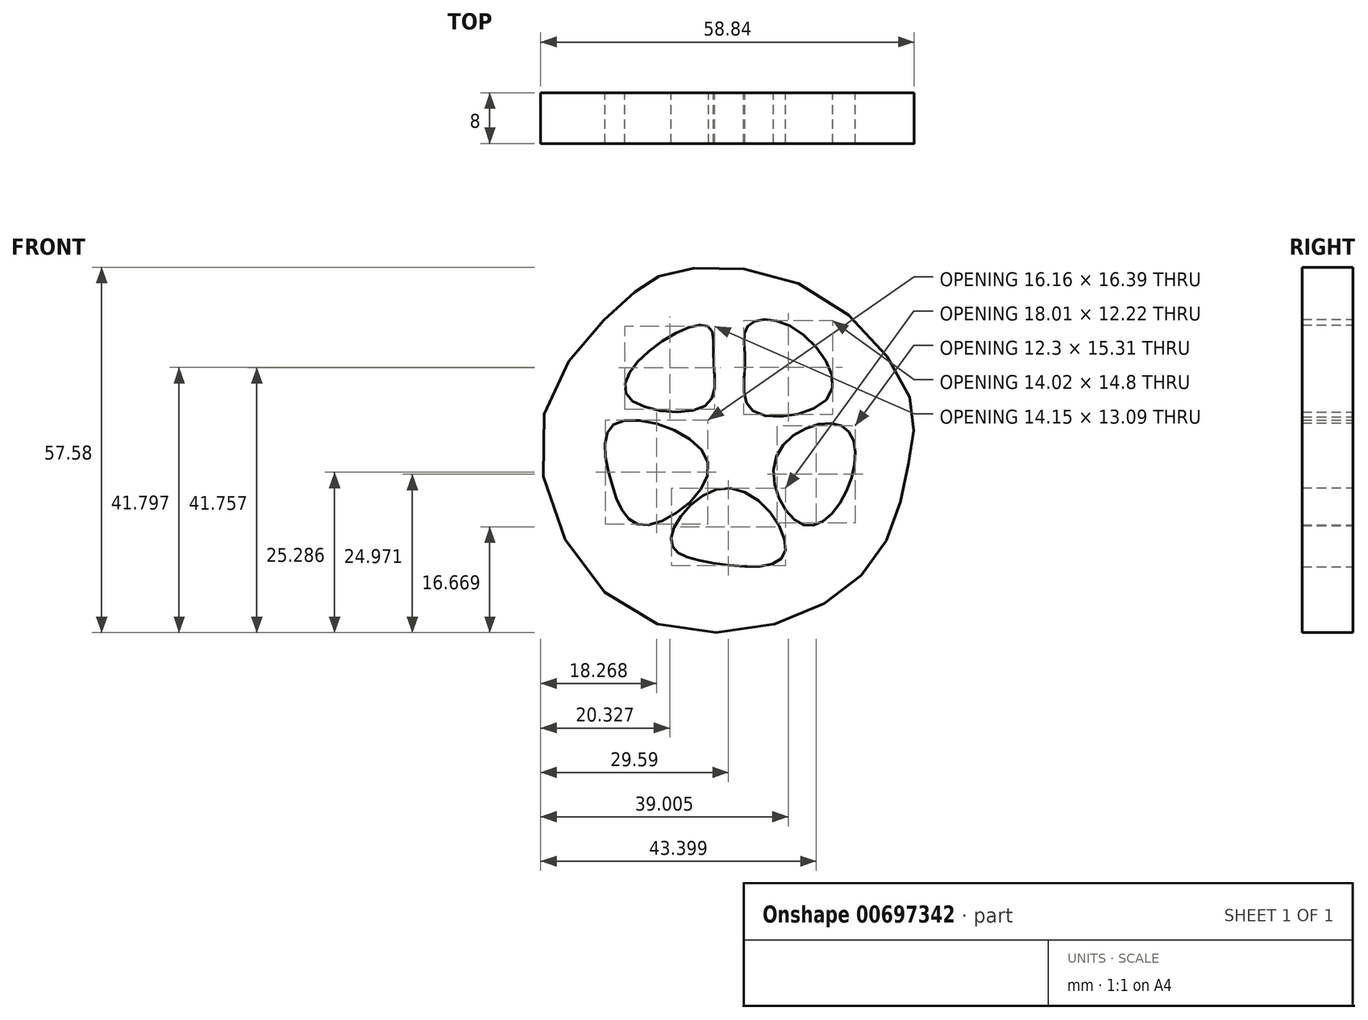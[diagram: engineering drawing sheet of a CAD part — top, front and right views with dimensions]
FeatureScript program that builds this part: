
annotation { "Feature Type Name" : "Feature", "Feature Type Description" : "" }
export const myFeature = defineFeature(function(context is Context, id is Id, definition is map)
    precondition{}
    {
        {
            var Q0;
            Q0=qCreatedBy(makeId("Front.planeOp"),FACE);
            var sketch = newSketch(context, id + "F0", { "sketchPlane" : qUnion([Q0])});
            skFitSpline(sketch, "E0", {"points": [v(-51.78, 50.56) * mm, v(-50.89, 45.19) * mm, v(-52.23, 38.02) * mm, v(-64.32, 39.37) * mm, v(-61.19, 46.53) * mm, v(-51.78, 50.56) * mm]});
            skFitSpline(sketch, "E1", {"points": [v(-45.52, 50.56) * mm, v(-45.96, 44.74) * mm, v(-44.62, 37.13) * mm, v(-32.53, 39.81) * mm, v(-38.8, 50.56) * mm, v(-45.52, 50.56) * mm]});
            skFitSpline(sketch, "E2", {"points": [v(-30.74, 34.89) * mm, v(-41.04, 29.96) * mm, v(-36.56, 19.22) * mm, v(-29.4, 25.93) * mm, v(-30.74, 34.89) * mm]});
            skFitSpline(sketch, "E3", {"points": [v(-48.2, 25.04) * mm, v(-57.6, 16.98) * mm, v(-51.78, 13.4) * mm, v(-39.7, 14.74) * mm, v(-48.2, 25.04) * mm]});
            skFitSpline(sketch, "E4", {"points": [v(-51.78, 29.07) * mm, v(-66.11, 35.34) * mm, v(-67, 25.93) * mm, v(-61.64, 19.22) * mm, v(-51.78, 29.07) * mm]});
            skFitSpline(sketch, "E5", {"points": [v(-20, 39.37) * mm, v(-20, 29.96) * mm, v(-23.57, 16.98) * mm, v(-36.56, 5.33) * mm, v(-64.32, 5.78) * mm, v(-77.76, 35.78) * mm, v(-64.32, 55.04) * mm, v(-57.6, 59.07) * mm, v(-36.56, 56.83) * mm, v(-20, 39.37) * mm]});
            skSolve(sketch);
        }
        {
            var Q0;
            Q0=qSketchRegion(id+"F0",true);
            extrude(context, id + "F1", {"entities" : qUnion([Q0]), "depth" : 8 * mm, "offsetDistance" : 25 * mm});
        }
    });
